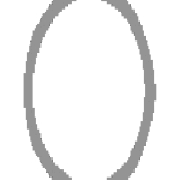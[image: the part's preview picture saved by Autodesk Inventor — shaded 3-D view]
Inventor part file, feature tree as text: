
AUTODESK INVENTOR PART (.ipt)
format: ipt  version: 2021 (Build 250183000, 183)  size: 112,128 bytes
history: native  units: in
note: dims shown in document units (in); Inventor stores cm internally (conversion verified against a paired STEP export)
features: other x4, sketch x3, plane x1
ambient origin geometry x8: Origin, YZ Plane, XZ Plane, XY Plane, X Axis, Y Axis, Z Axis, Center Point
bodies: Solid1 (feature_tree), Body (feature_tree)
feature tree (8):
  other  "Driven Length"
  other  "Frame Generator"
  other  "Start Plane"
  other  "End Plane"
  sketch  "Sketch"  dims[d2=22.3842in d4=-0.0in d5=22.3842in d6=0.12in d7=0.0in d8=90.0deg d9=22.3842in]
  sketch  "Sketch2"  dims[d0=1.0in]
  plane  "Work Plane3"
  sketch  "Sketch3"  dims[d1=0.065in]
